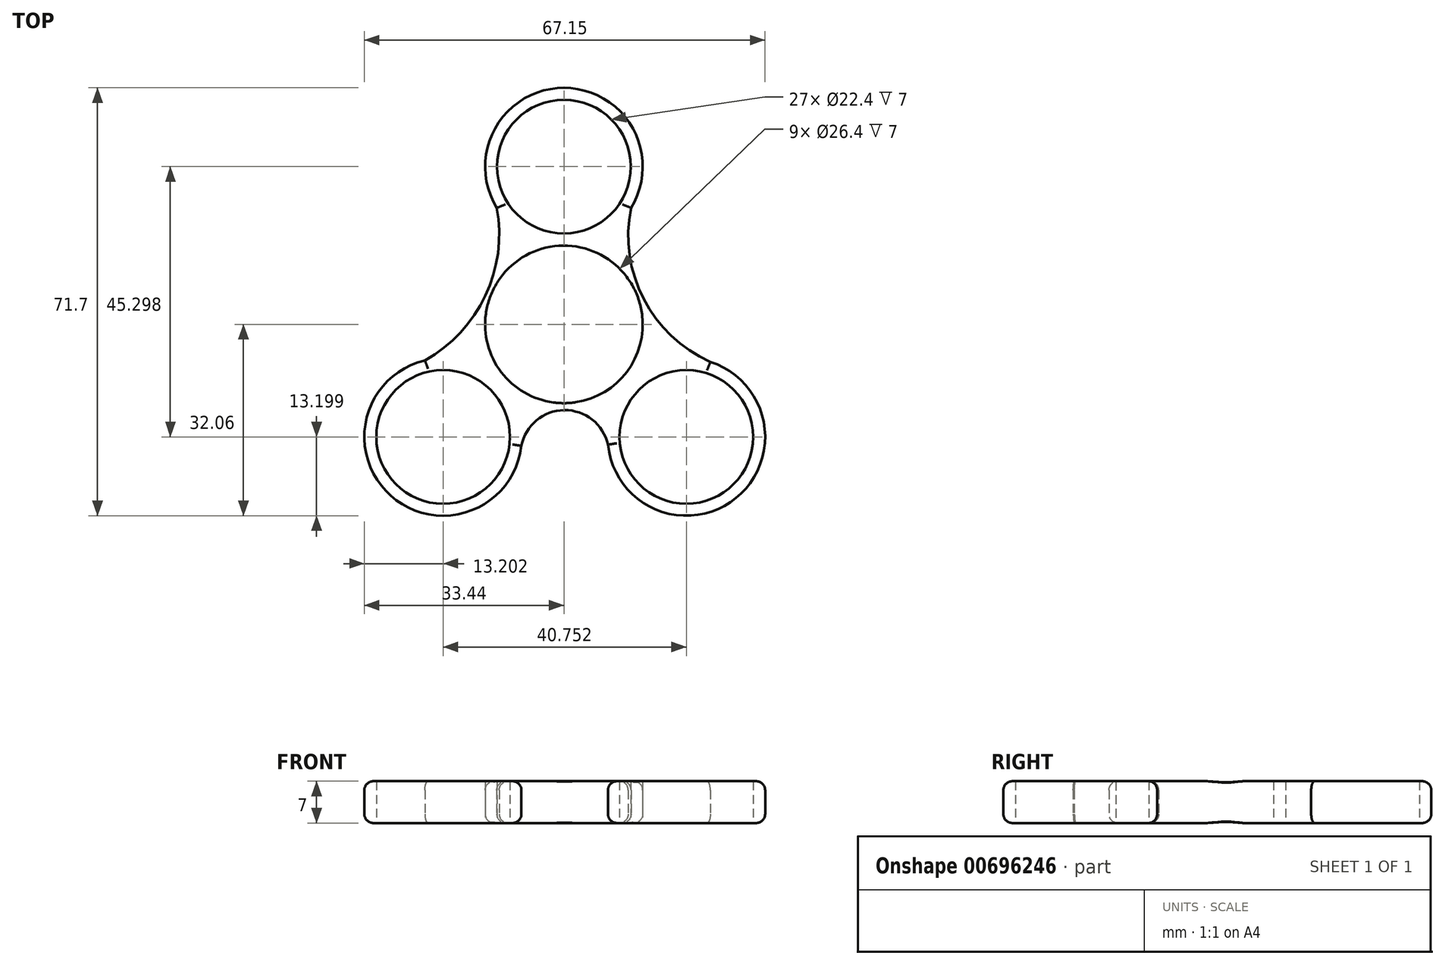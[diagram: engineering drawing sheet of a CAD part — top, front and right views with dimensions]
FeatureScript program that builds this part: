
annotation { "Feature Type Name" : "Feature", "Feature Type Description" : "" }
export const myFeature = defineFeature(function(context is Context, id is Id, definition is map)
    precondition{}
    {
        {
            var Q0;
            Q0=qCreatedBy(makeId("Top.planeOp"),FACE);
            var sketch = newSketch(context, id + "F0", { "sketchPlane" : qUnion([Q0])});
            skCircle(sketch, "E0", {"center": v(0, 0) * mm, "radius": 11.2 * mm});
            skCircle(sketch, "E1", {"center": v(0, 0) * mm, "radius": 13.2 * mm});
            skCircle(sketch, "E2", {"center": v(0, 26.44) * mm, "radius": 11.2 * mm});
            skCircle(sketch, "E3", {"center": v(0, 26.44) * mm, "radius": 13.2 * mm});
            skCircle(sketch, "E4", {"center": v(20.51, -18.86) * mm, "radius": 11.2 * mm});
            skCircle(sketch, "E5", {"center": v(20.51, -18.86) * mm, "radius": 13.2 * mm});
            skCircle(sketch, "E6", {"center": v(-20.24, -18.86) * mm, "radius": 11.2 * mm});
            skCircle(sketch, "E7", {"center": v(-20.24, -18.86) * mm, "radius": 13.2 * mm});
            skArc(sketch, "E8", {"start": v(11.24, 19.52) * mm, "mid": v(13.35, 4.28) * mm, "end": v(24.53, -6.29) * mm});
            skArc(sketch, "E9", {"start": v(-23.3, -6.02) * mm, "mid": v(-13.15, 4.8) * mm, "end": v(-11.25, 19.53) * mm});
            skArc(sketch, "E10", {"start": v(7.54, -21.3) * mm, "mid": v(0.25, -14.37) * mm, "end": v(-7.23, -21.1) * mm});
            skSolve(sketch);
        }
        {
            var Q0;
            Q0 = qSketchRegion(id + "F0", true);
            extrude(context, id + "F1", {"entities" : qUnion([Q0]), "depth" : 7 * mm, "offsetDistance" : 25 * mm});
        }
        {
            var Q0;
            Q0=makeQuery(id+"F1.opExtrude","CAP_EDGE",EDGE,{"disambiguationData":[OSD([sQuery(id+"F0.wireOp",EDGE,"E10")])],"isStart":false});
            var Q1;
            Q1=makeQuery(id+"F1.opExtrude","CAP_EDGE",EDGE,{"disambiguationData":[OSD([sQuery(id+"F0.wireOp",EDGE,"E7")])],"isStart":false});
            var Q2;
            Q2=makeQuery(id+"F1.opExtrude","CAP_EDGE",EDGE,{"disambiguationData":[OSD([sQuery(id+"F0.wireOp",EDGE,"E9")])],"isStart":false});
            var Q3;
            Q3=makeQuery(id+"F1.opExtrude","CAP_EDGE",EDGE,{"disambiguationData":[OSD([sQuery(id+"F0.wireOp",EDGE,"E3")])],"isStart":false});
            var Q4;
            Q4=makeQuery(id+"F1.opExtrude","CAP_EDGE",EDGE,{"disambiguationData":[OSD([sQuery(id+"F0.wireOp",EDGE,"E8")])],"isStart":false});
            var Q5;
            Q5=makeQuery(id+"F1.opExtrude","CAP_EDGE",EDGE,{"disambiguationData":[OSD([sQuery(id+"F0.wireOp",EDGE,"E5")])],"isStart":false});
            fillet(context, id + "F2", {"entities" : qUnion([Q0, Q1, Q2, Q3, Q4, Q5]), "radius" : 1.5 * mm, "tangentPropagation" : true, "allowEdgeOverflow" : false});
        }
        {
            var Q0;
            Q0=makeQuery(id+"F1.opExtrude","CAP_EDGE",EDGE,{"disambiguationData":[OSD([sQuery(id+"F0.wireOp",EDGE,"E7")])],"isStart":true});
            var Q1;
            Q1=makeQuery(id+"F1.opExtrude","CAP_EDGE",EDGE,{"disambiguationData":[OSD([sQuery(id+"F0.wireOp",EDGE,"E3")])],"isStart":true});
            var Q2;
            Q2=makeQuery(id+"F1.opExtrude","CAP_EDGE",EDGE,{"disambiguationData":[OSD([sQuery(id+"F0.wireOp",EDGE,"E5")])],"isStart":true});
            var Q3;
            Q3=makeQuery(id+"F1.opExtrude","CAP_EDGE",EDGE,{"disambiguationData":[OSD([sQuery(id+"F0.wireOp",EDGE,"E9")])],"isStart":true});
            var Q4;
            Q4=makeQuery(id+"F1.opExtrude","CAP_EDGE",EDGE,{"disambiguationData":[OSD([sQuery(id+"F0.wireOp",EDGE,"E10")])],"isStart":true});
            var Q5;
            Q5=makeQuery(id+"F1.opExtrude","CAP_EDGE",EDGE,{"disambiguationData":[OSD([sQuery(id+"F0.wireOp",EDGE,"E8")])],"isStart":true});
            fillet(context, id + "F3", {"entities" : qUnion([Q0, Q1, Q2, Q3, Q4, Q5]), "radius" : 1.5 * mm, "tangentPropagation" : true, "allowEdgeOverflow" : false});
        }
    });
